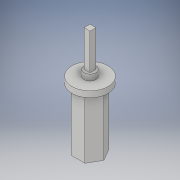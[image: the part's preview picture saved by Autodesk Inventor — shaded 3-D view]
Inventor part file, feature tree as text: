
AUTODESK INVENTOR PART (.ipt)
format: ipt  version: 2019 (Build 230136000, 136)  size: 123,392 bytes
history: native  units: in
note: dims shown in document units (in); Inventor stores cm internally (conversion verified against a paired STEP export)
features: extrude x4, sketch x4
ambient origin geometry x8: Origin, YZ Plane, XZ Plane, XY Plane, X Axis, Y Axis, Z Axis, Center Point
bodies: Solid1 (feature_tree)
feature tree (8):
  extrude  "Extrusion1"  TaperAngle=0.0deg  [1 undecoded]
  extrude  "Extrusion2"  Depth=0.75in
  extrude  "Extrusion3"  Depth=0.25in
  extrude  "Extrusion4"  Depth=0.125in
  sketch  "Sketch1"  dims[d0=0.5in d1=0.0in]
  sketch  "Sketch2"  dims[d2=1.25in d3=0.0in d4=0.75in]
  sketch  "Sketch3"  dims[d5=0.125in d6=0.0in d7=0.25in]
  sketch  "Sketch4"  dims[d8=0.125in d9=0.0in d10=0.125in d11=0.125in d12=0.75in d13=0.0in]
note: 1 required parameter value undecoded (feature->parameter linkage not recoverable at this tier; creation-order binding heuristic only, values carry confidence <= 0.55)
